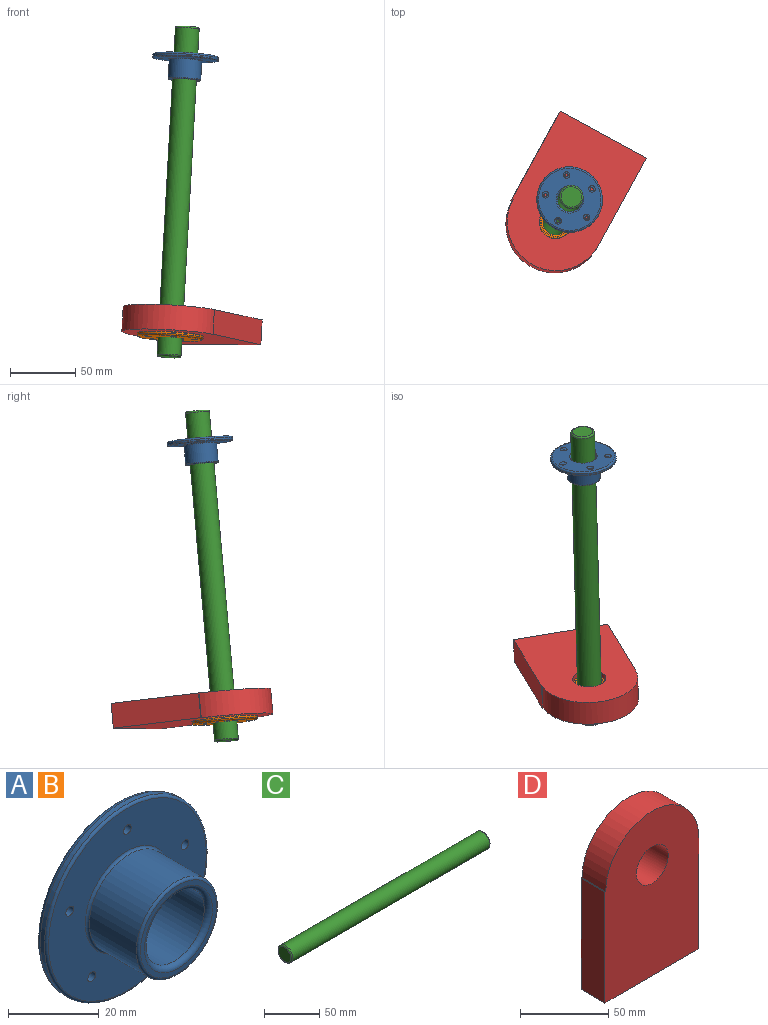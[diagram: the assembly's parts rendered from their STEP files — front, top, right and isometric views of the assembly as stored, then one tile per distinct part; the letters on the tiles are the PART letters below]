
ASSEMBLY  parts=4 mates=3
PART A: 22 faces, bbox 54.5x19.1x54.5 mm
  f0: cone r=2.49mm half-angle=45deg, axis (0,1,0), area 20.9mm2, adj f1,f10
  f1: cylinder r=1.22mm len=2.43mm, axis (0,-1,0), area 14.5mm2, adj f0,f9
  f2: cone r=2.49mm half-angle=45deg, axis (0,1,0), area 20.9mm2, adj f3,f10
  f3: cylinder r=1.22mm len=2.43mm, axis (0,-1,0), area 14.5mm2, adj f2,f9
  f4: cone r=2.49mm half-angle=45deg, axis (0,1,0), area 20.9mm2, adj f5,f10
  f5: cylinder r=1.22mm len=2.43mm, axis (0,-1,0), area 14.5mm2, adj f4,f9
  f6: cone r=2.49mm half-angle=45deg, axis (0,1,0), area 20.9mm2, adj f7,f10
  f7: cylinder r=1.22mm len=2.43mm, axis (0,-1,0), area 14.5mm2, adj f6,f9
  f8: cylinder r=25.18mm len=50.36mm, axis (0,1,0), area 200.9mm2, adj f16,f20
  f9: plane 49.09x49.09mm, normal (0,-1,0), area 1329mm2, adj f1,f3,f5,f7,f14,f20,f21
  f10: plane 47.82x47.82mm, normal (0,1,0), area 1347.6mm2, adj f0,f2,f4,f6,f15,f16,f17
  f11: plane 23.69x23.69mm, normal (0,-1,0), area 89.4mm2, adj f18,f19
  f12: cylinder r=12.48mm len=24.96mm, axis (0,1,0), area 1145.1mm2, adj f19,f21
  f13: cylinder r=9.3mm len=18.61mm, axis (0,-1,0), area 965.1mm2, adj f17,f18
  f14: cylinder r=1.22mm len=2.43mm, axis (0,-1,0), area 14.5mm2, adj f9,f15
  f15: cone r=2.49mm half-angle=45deg, axis (0,1,0), area 20.9mm2, adj f10,f14
  f16: torus R=23.91mm, axis (0,-1,0), area 309.8mm2, adj f8,f10
  f17: cone r=10.57mm half-angle=45deg, axis (0,1,0), area 112.2mm2, adj f10,f13
  f18: torus R=10.57mm, axis (0,-1,0), area 122.4mm2, adj f11,f13
  f19: torus R=11.84mm, axis (0,-1,0), area 76.8mm2, adj f11,f12
  f20: torus R=24.54mm, axis (0,-1,0), area 156.4mm2, adj f8,f9
  f21: torus R=13.11mm, axis (0,-1,0), area 79.7mm2, adj f9,f12
PART B: same geometry as A
PART C: 5 faces, bbox 254x19.8x19.8 mm
  f0: cylinder r=9.13mm len=251.46mm, axis (-1,0,0), area 14421.7mm2, adj f3,f4
  f1: plane 15.72x15.72mm, normal (1,0,0), area 194mm2, adj f4
  f2: plane 15.72x15.72mm, normal (-1,0,0), area 194mm2, adj f3
  f3: torus R=7.86mm, axis (1,0,0), area 108.6mm2, adj f0,f2
  f4: torus R=7.86mm, axis (1,0,0), area 108.6mm2, adj f0,f1
PART D: 9 faces, bbox 75.2x19.1x113.9 mm
  f0: plane 19.05x0.08mm, normal (0,0,1), area 1.5mm2, adj f4,f5,f6,f8
  f1: plane 19.05x0.71mm, normal (0,0,1), area 13.5mm2, adj f2,f5,f6,f8
  f2: plane 76.76x19.05mm, normal (-1,0,0), area 1462.2mm2, adj f1,f3,f5,f6
  f3: plane 75.16x19.05mm, normal (0,0,-1), area 1431.7mm2, adj f2,f4,f5,f6
  f4: plane 76.76x19.05mm, normal (1,0,0), area 1462.2mm2, adj f0,f3,f5,f6
  f5: plane 113.94x75.16mm, normal (0,-1,0), area 7434mm2, adj f0,f1,f2,f3,f4,f7,f8
  f6: plane 113.94x75.16mm, normal (0,1,0), area 7434mm2, adj f0,f1,f2,f3,f4,f7,f8
  f7: cylinder r=12.7mm len=25.4mm, axis (0,1,0), area 1520.1mm2, adj f5,f6
  f8: cylinder r=37.18mm len=74.37mm, axis (0,1,0), area 2225.4mm2, adj f0,f1,f5,f6
PLACE A rot(axis=(0.93,-0.24,-0.27),88deg) t=(-66.52,82.59,147.86)mm fixed
PLACE B rot(axis=(-0.95,0.24,-0.21),99deg) t=(-78.54,63.41,-68.84)mm
PLACE C rot(axis=(0.19,0.94,-0.28),95.4deg) t=(-72.33,73.32,43.1)mm fixed
PLACE D rot(axis=(0.93,-0.24,-0.27),88deg) t=(-77.31,65.37,-46.73)mm fixed
MATE slider C.f0 <-> B.f13  axis (-0.06,-0.09,-0.99) through (-79.34,62.14,-83.21)mm
MATE cylindrical C.f0 <-> D.f7  axis (0.06,0.09,0.99) through (-65.33,84.5,169.41)mm
MATE pin_slot D.f8 <-> B.f8  axis (-0.06,-0.09,-0.99) through (-78.36,63.69,-65.68)mm
